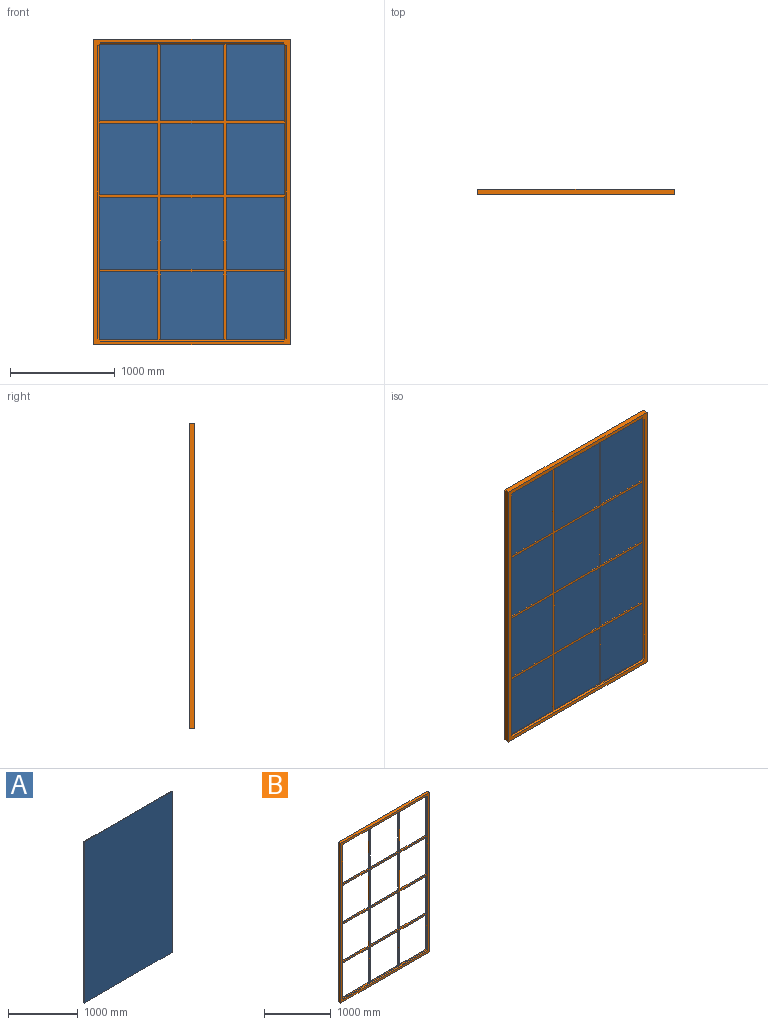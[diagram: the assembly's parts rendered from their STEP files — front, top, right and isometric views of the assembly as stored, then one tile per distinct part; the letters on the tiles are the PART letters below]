
ASSEMBLY  parts=2 mates=1
PART A: 6 faces, bbox 1773.8x10x2821.5 mm
  f0: plane 2821.53x10mm, normal (1,0,0), area 28215.2mm2, adj f1,f3,f4,f5
  f1: plane 1773.79x10mm, normal (0,0,1), area 17737.9mm2, adj f0,f2,f4,f5
  f2: plane 2821.53x10mm, normal (-1,0,0), area 28215.2mm2, adj f1,f3,f4,f5
  f3: plane 1773.79x10mm, normal (0,0,-1), area 17737.9mm2, adj f0,f2,f4,f5
  f4: plane 2821.53x1773.79mm, normal (0,-1,0), area 5004792.8mm2, adj f0,f1,f2,f3
  f5: plane 2821.53x1773.79mm, normal (0,1,0), area 5004792.8mm2, adj f0,f1,f2,f3
PART B: 76 faces, bbox 1873.8x50x2921.5 mm
  f0: plane 684x24mm, normal (1,0,0), area 16416mm2, adj f38,f48,f68,f75
  f1: plane 715.53x24mm, normal (-1,0,0), area 17172.6mm2, adj f36,f45,f46,f71
  f2: plane 728.53x24mm, normal (1,0,0), area 17484.6mm2, adj f19,f53,f55,f73
  f3: plane 728.53x24mm, normal (-1,0,0), area 17484.6mm2, adj f21,f53,f55,f74
  f4: plane 728.53x24mm, normal (-1,0,0), area 17484.6mm2, adj f19,f53,f55,f73
  f5: plane 728.53x24mm, normal (1,0,0), area 17484.6mm2, adj f24,f53,f55,f71
  f6: plane 684x24mm, normal (1,0,0), area 16416mm2, adj f38,f48,f62,f69
  f7: plane 684x24mm, normal (-1,0,0), area 16416mm2, adj f36,f45,f65,f70
  f8: plane 684x24mm, normal (1,0,0), area 16416mm2, adj f53,f55,f67,f72
  f9: plane 684x24mm, normal (-1,0,0), area 16416mm2, adj f53,f55,f68,f75
  f10: plane 684x24mm, normal (-1,0,0), area 16416mm2, adj f53,f55,f67,f72
  f11: plane 684x24mm, normal (1,0,0), area 16416mm2, adj f53,f55,f65,f70
  f12: plane 634x24mm, normal (1,0,0), area 15216mm2, adj f38,f39,f48,f63
  f13: plane 684x24mm, normal (-1,0,0), area 16416mm2, adj f36,f45,f59,f64
  f14: plane 684x24mm, normal (1,0,0), area 16416mm2, adj f53,f55,f61,f66
  f15: plane 684x24mm, normal (-1,0,0), area 16416mm2, adj f53,f55,f62,f69
  f16: plane 684x24mm, normal (-1,0,0), area 16416mm2, adj f53,f55,f61,f66
  f17: plane 684x24mm, normal (1,0,0), area 16416mm2, adj f53,f55,f59,f64
  f18: plane 598.61x24mm, normal (0,0,1), area 14366.6mm2, adj f32,f40,f52,f56
  f19: plane 598.61x24mm, normal (0,0,-1), area 14366.6mm2, adj f2,f4,f37,f51
  f20: plane 548.59x24mm, normal (0,0,1), area 13166.2mm2, adj f32,f39,f40,f54
  f21: plane 548.59x24mm, normal (0,0,-1), area 13166.2mm2, adj f3,f37,f47,f51
  f22: plane 2921.53x1873.79mm, normal (0,1,0), area 350729.3mm2, adj f27,f28,f29,f30,f32,f33,f34,f36
  f23: plane 2921.53x1873.79mm, normal (0,-1,0), area 350729.3mm2, adj f27,f28,f29,f30,f40,f41,f44,f45
  f24: plane 548.59x24mm, normal (0,0,-1), area 13166.2mm2, adj f5,f37,f46,f51
  f25: plane 634x24mm, normal (-1,0,0), area 15216mm2, adj f35,f36,f45,f58
  f26: plane 548.59x24mm, normal (0,0,1), area 13166.2mm2, adj f32,f35,f40,f57
  f27: plane 2921.53x50mm, normal (1,0,0), area 146076.2mm2, adj f22,f23,f28,f30
  f28: plane 1873.79x50mm, normal (0,0,1), area 93689.5mm2, adj f22,f23,f27,f29
  f29: plane 2921.53x50mm, normal (-1,0,0), area 146076.2mm2, adj f22,f23,f28,f30
  f30: plane 1873.79x50mm, normal (0,0,-1), area 93689.5mm2, adj f22,f23,f27,f29
  f31: plane 715.53x24mm, normal (1,0,0), area 17172.6mm2, adj f38,f47,f48,f74
  f32: plane 1747.79x13mm, normal (0,0.71,0.71), area 32132.7mm2, adj f18,f20,f22,f26,f33,f34,f53
  f33: plane 26x26mm, normal (-0.58,0.58,0.58), area 439.1mm2, adj f22,f32,f35,f36
  f34: plane 26x26mm, normal (0.58,0.58,0.58), area 439.1mm2, adj f22,f32,f38,f39
  f35: plane 24x13mm, normal (-0.71,0,0.71), area 441.2mm2, adj f25,f26,f33,f41
  f36: plane 2795.53x13mm, normal (-0.71,0.71,0), area 51395.1mm2, adj f1,f7,f13,f22,f25,f33,f42,f53
  f37: plane 1747.79x13mm, normal (0,0.71,-0.71), area 32132.7mm2, adj f19,f21,f22,f24,f42,f43,f53
  f38: plane 2795.53x13mm, normal (0.71,0.71,0), area 51395.1mm2, adj f0,f6,f12,f22,f31,f34,f43,f53
  f39: plane 24x13mm, normal (0.71,0,0.71), area 441.2mm2, adj f12,f20,f34,f44
  f40: plane 1747.79x13mm, normal (0,-0.71,0.71), area 32132.7mm2, adj f18,f20,f23,f26,f41,f44,f55
  f41: plane 26x26mm, normal (-0.58,-0.58,0.58), area 439.1mm2, adj f23,f35,f40,f45
  f42: plane 26x26mm, normal (-0.58,0.58,-0.58), area 439.1mm2, adj f22,f36,f37,f46
  f43: plane 26x26mm, normal (0.58,0.58,-0.58), area 439.1mm2, adj f22,f37,f38,f47
  f44: plane 26x26mm, normal (0.58,-0.58,0.58), area 439.1mm2, adj f23,f39,f40,f48
  f45: plane 2795.53x13mm, normal (-0.71,-0.71,0), area 51395.1mm2, adj f1,f7,f13,f23,f25,f41,f49,f55
  f46: plane 24x13mm, normal (-0.71,0,-0.71), area 441.2mm2, adj f1,f24,f42,f49
  f47: plane 24x13mm, normal (0.71,0,-0.71), area 441.2mm2, adj f21,f31,f43,f50
  f48: plane 2795.53x13mm, normal (0.71,-0.71,0), area 51395.1mm2, adj f0,f6,f12,f23,f31,f44,f50,f55
  f49: plane 26x26mm, normal (-0.58,-0.58,-0.58), area 439.1mm2, adj f23,f45,f46,f51
  f50: plane 26x26mm, normal (0.58,-0.58,-0.58), area 439.1mm2, adj f23,f47,f48,f51
  f51: plane 1747.79x13mm, normal (0,-0.71,-0.71), area 32132.7mm2, adj f19,f21,f23,f24,f49,f50,f55
  f52: plane 647x24mm, normal (1,0,0), area 15528mm2, adj f18,f53,f55,f60
  f53: plane 2821.53x1773.79mm, normal (0,1,0), area 281018.9mm2, adj f2,f3,f4,f5,f8,f9,f10,f11
  f54: plane 647x24mm, normal (-1,0,0), area 15528mm2, adj f20,f53,f55,f63
  f55: plane 2821.53x1773.79mm, normal (0,-1,0), area 281018.9mm2, adj f2,f3,f4,f5,f8,f9,f10,f11
  f56: plane 647x24mm, normal (-1,0,0), area 15528mm2, adj f18,f53,f55,f60
  f57: plane 647x24mm, normal (1,0,0), area 15528mm2, adj f26,f53,f55,f58
  f58: plane 561.59x24mm, normal (0,0,-1), area 13478.2mm2, adj f25,f53,f55,f57
  f59: plane 561.59x24mm, normal (0,0,1), area 13478.2mm2, adj f13,f17,f53,f55
  f60: plane 598.61x24mm, normal (0,0,-1), area 14366.6mm2, adj f52,f53,f55,f56
  f61: plane 598.61x24mm, normal (0,0,1), area 14366.6mm2, adj f14,f16,f53,f55
  f62: plane 561.59x24mm, normal (0,0,1), area 13478.2mm2, adj f6,f15,f53,f55
  f63: plane 561.59x24mm, normal (0,0,-1), area 13478.2mm2, adj f12,f53,f54,f55
  f64: plane 561.59x24mm, normal (0,0,-1), area 13478.2mm2, adj f13,f17,f53,f55
  f65: plane 561.59x24mm, normal (0,0,1), area 13478.2mm2, adj f7,f11,f53,f55
  f66: plane 598.61x24mm, normal (0,0,-1), area 14366.6mm2, adj f14,f16,f53,f55
  f67: plane 598.61x24mm, normal (0,0,1), area 14366.6mm2, adj f8,f10,f53,f55
  f68: plane 561.59x24mm, normal (0,0,1), area 13478.2mm2, adj f0,f9,f53,f55
  f69: plane 561.59x24mm, normal (0,0,-1), area 13478.2mm2, adj f6,f15,f53,f55
  f70: plane 561.59x24mm, normal (0,0,-1), area 13478.2mm2, adj f7,f11,f53,f55
  f71: plane 561.59x24mm, normal (0,0,1), area 13478.2mm2, adj f1,f5,f53,f55
  f72: plane 598.61x24mm, normal (0,0,-1), area 14366.6mm2, adj f8,f10,f53,f55
  f73: plane 598.61x24mm, normal (0,0,1), area 14366.6mm2, adj f2,f4,f53,f55
  f74: plane 561.59x24mm, normal (0,0,1), area 13478.2mm2, adj f3,f31,f53,f55
  f75: plane 561.59x24mm, normal (0,0,-1), area 13478.2mm2, adj f0,f9,f53,f55
PLACE A t=(0,-20,0)mm
PLACE B at identity
MATE fastened A.f3 <-> B.f18  axis (0,0,-1) through (0,-25,-1410.76)mm
